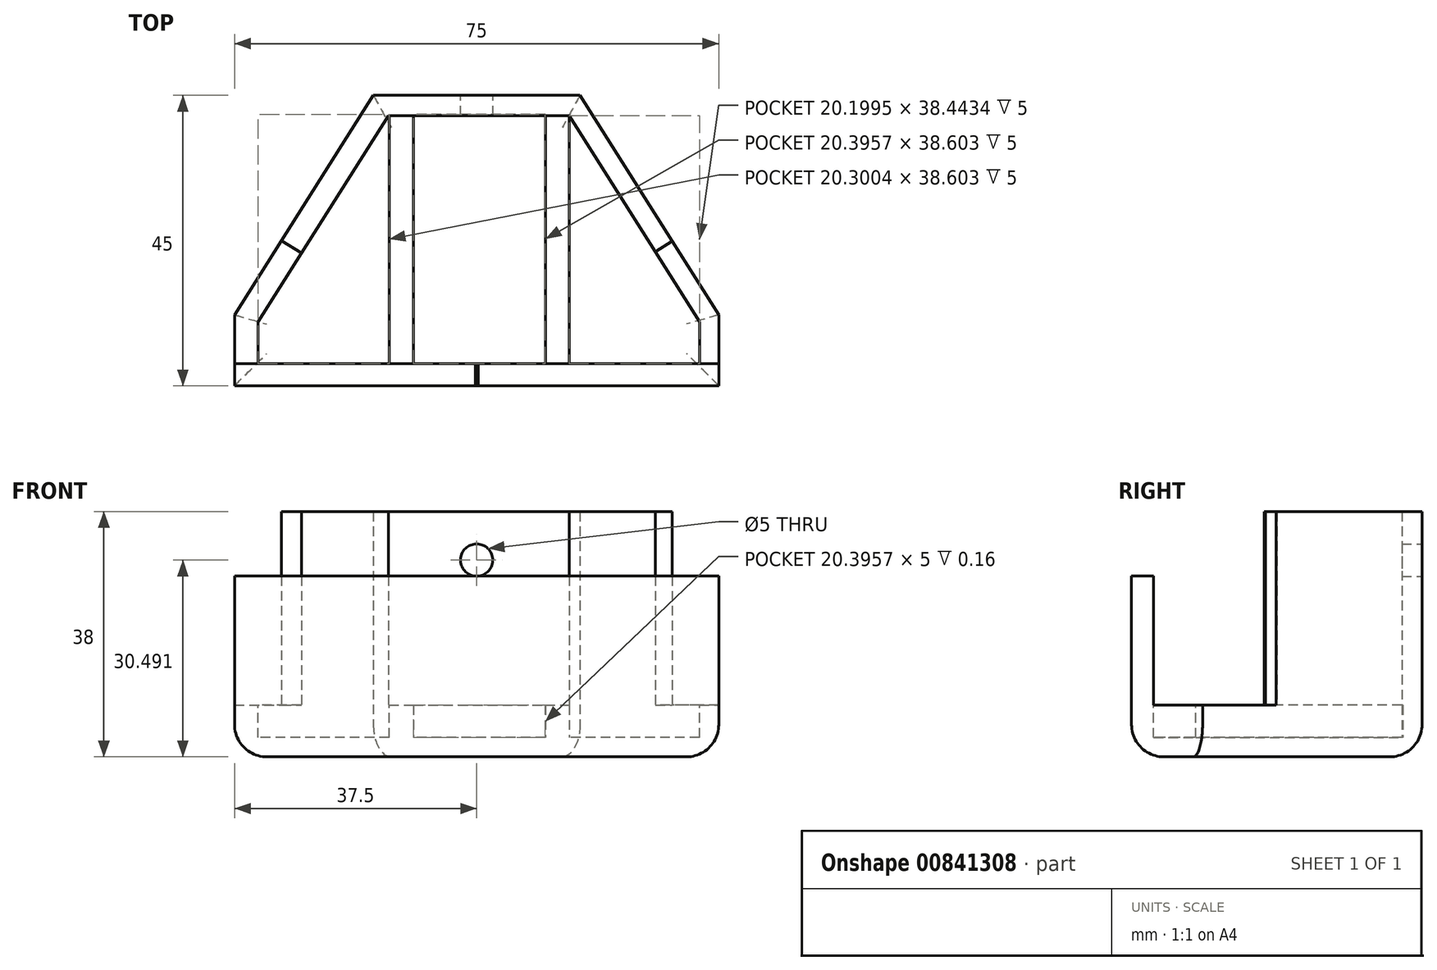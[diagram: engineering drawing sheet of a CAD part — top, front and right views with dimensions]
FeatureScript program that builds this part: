
annotation { "Feature Type Name" : "Feature", "Feature Type Description" : "" }
export const myFeature = defineFeature(function(context is Context, id is Id, definition is map)
    precondition{}
    {
        {
            var Q0;
            Q0=qCreatedBy(makeId("Top.planeOp"),FACE);
            var sketch = newSketch(context, id + "F0", { "sketchPlane" : qUnion([Q0])});
            skLineSegment(sketch, "E0.bottom", {"start": v(37.5, -22.5) * mm, "end": v(-37.5, -22.5) * mm});
            skLineSegment(sketch, "E0.top", {"start": v(16, 22.5) * mm, "end": v(-16, 22.5) * mm});
            skLineSegment(sketch, "E0.left", {"start": v(37.5, -22.5) * mm, "end": v(37.5, -11.5) * mm});
            skLineSegment(sketch, "E0.right", {"start": v(-37.5, -22.5) * mm, "end": v(-37.5, -11.5) * mm});
            skPoint(sketch, "E0.middle", {"position": v(0, 0) * mm});
            skLineSegment(sketch, "E1", {"start": v(-37.5, -11.5) * mm, "end": v(-16, 22.5) * mm});
            skLineSegment(sketch, "E2", {"start": v(37.5, -11.5) * mm, "end": v(16, 22.5) * mm});
            skPoint(sketch, "E3.orphan", {"position": v(-37.5, 22.5) * mm});
            skPoint(sketch, "E4.orphan", {"position": v(37.5, 22.5) * mm});
            skSolve(sketch);
        }
        {
            var Q0;
            Q0=makeQuery(id+"F0.imprint","IMPRINT",FACE,{"disambiguationData":[TD([[makeQuery(id+"F0.imprint","IMPRINT",EDGE,{"derivedFrom":sQuery(id+"F0.wireOp",EDGE,"E0.bottom")}),-1.0]])]});
            extrude(context, id + "F1", {"entities" : qUnion([Q0]), "depth" : 8 * mm, "offsetDistance" : 25 * mm});
        }
        {
            var Q0;
            Q0=makeQuery(id+"F1.opExtrude","CAP_FACE",FACE,{"disambiguationData":[OSD([sQuery(id+"F0.wireOp",EDGE,"E0.bottom"),sQuery(id+"F0.wireOp",EDGE,"E0.top"),sQuery(id+"F0.wireOp",EDGE,"E0.left"),sQuery(id+"F0.wireOp",EDGE,"E0.right"),sQuery(id+"F0.wireOp",EDGE,"E1"),sQuery(id+"F0.wireOp",EDGE,"E2")])],"isStart":false});
            var sketch = newSketch(context, id + "F2", { "sketchPlane" : qUnion([Q0])});
            skLineSegment(sketch, "E5", {"start": v(-33.85, -12.58) * mm, "end": v(-33.85, -19.08) * mm});
            skLineSegment(sketch, "E6", {"start": v(-33.85, -19.08) * mm, "end": v(34.5, -19.08) * mm});
            skLineSegment(sketch, "E7", {"start": v(34.5, -19.08) * mm, "end": v(34.5, -12.58) * mm});
            skLineSegment(sketch, "E8", {"start": v(34.5, -12.58) * mm, "end": v(14.2, 19.53) * mm});
            skLineSegment(sketch, "E9", {"start": v(14.2, 19.53) * mm, "end": v(-13.55, 19.53) * mm});
            skLineSegment(sketch, "E10", {"start": v(-13.55, 19.53) * mm, "end": v(-33.85, -12.58) * mm});
            skSolve(sketch);
        }
        {
            var Q0;
            Q0 = qSketchRegion(id + "F2", true);
            extrude(context, id + "F3", {"entities" : qUnion([Q0]), "operationType" : NewBodyOperationType.REMOVE, "oppositeDirection" : true, "depth" : 5 * mm, "offsetDistance" : 25 * mm});
        }
        {
            var Q0;
            Q0=makeQuery(id+"F3.boolean.opBoolean","COPY",FACE,{"derivedFrom":makeQuery(id+"F3.opExtrude","CAP_FACE",FACE,{"disambiguationData":[OSD([sQuery(id+"F2.wireOp",EDGE,"E5"),sQuery(id+"F2.wireOp",EDGE,"E6"),sQuery(id+"F2.wireOp",EDGE,"E7"),sQuery(id+"F2.wireOp",EDGE,"E8"),sQuery(id+"F2.wireOp",EDGE,"E9"),sQuery(id+"F2.wireOp",EDGE,"E10")])],"isStart":false})});
            var sketch = newSketch(context, id + "F4", { "sketchPlane" : qUnion([Q0])});
            skLineSegment(sketch, "E11.bottom", {"start": v(-9.77, 19.53) * mm, "end": v(-13.55, 19.53) * mm});
            skLineSegment(sketch, "E11.top", {"start": v(-9.77, -19.08) * mm, "end": v(-13.55, -19.08) * mm});
            skLineSegment(sketch, "E11.left", {"start": v(-9.77, 19.53) * mm, "end": v(-9.77, -19.08) * mm});
            skLineSegment(sketch, "E11.right", {"start": v(-13.55, 19.53) * mm, "end": v(-13.55, -19.08) * mm});
            skLineSegment(sketch, "E12.bottom", {"start": v(10.62, 19.53) * mm, "end": v(14.3, 19.53) * mm});
            skLineSegment(sketch, "E12.top", {"start": v(10.62, -19.08) * mm, "end": v(14.3, -19.08) * mm});
            skLineSegment(sketch, "E12.left", {"start": v(10.62, 19.53) * mm, "end": v(10.62, -19.08) * mm});
            skLineSegment(sketch, "E12.right", {"start": v(14.3, 19.53) * mm, "end": v(14.3, -19.08) * mm});
            skSolve(sketch);
        }
        {
            var Q0;
            Q0 = qSketchRegion(id + "F4", true);
            extrude(context, id + "F5", {"entities" : qUnion([Q0]), "operationType" : NewBodyOperationType.ADD, "depth" : 5 * mm, "offsetDistance" : 25 * mm});
        }
        {
            var Q0;
            Q0=makeQuery(id+"F5.boolean.opBoolean","MERGE",FACE,{"derivedFrom":[makeQuery(id+"F1.opExtrude","CAP_FACE",FACE,{"disambiguationData":[OSD([sQuery(id+"F0.wireOp",EDGE,"E0.bottom"),sQuery(id+"F0.wireOp",EDGE,"E0.top"),sQuery(id+"F0.wireOp",EDGE,"E0.left"),sQuery(id+"F0.wireOp",EDGE,"E0.right"),sQuery(id+"F0.wireOp",EDGE,"E1"),sQuery(id+"F0.wireOp",EDGE,"E2")])],"isStart":false}),makeQuery(id+"F5.opExtrude","CAP_FACE",FACE,{"disambiguationData":[OSD([sQuery(id+"F4.wireOp",EDGE,"E11.bottom"),sQuery(id+"F4.wireOp",EDGE,"E11.top"),sQuery(id+"F4.wireOp",EDGE,"E11.left"),sQuery(id+"F4.wireOp",EDGE,"E11.right")])],"isStart":false}),makeQuery(id+"F5.opExtrude","CAP_FACE",FACE,{"disambiguationData":[OSD([sQuery(id+"F4.wireOp",EDGE,"E12.bottom"),sQuery(id+"F4.wireOp",EDGE,"E12.top"),sQuery(id+"F4.wireOp",EDGE,"E12.left"),sQuery(id+"F4.wireOp",EDGE,"E12.right")])],"isStart":false})]});
            var sketch = newSketch(context, id + "F6", { "sketchPlane" : qUnion([Q0])});
            skLineSegment(sketch, "E13.bottom", {"start": v(-37.5, -22.5) * mm, "end": v(37.5, -22.5) * mm});
            skLineSegment(sketch, "E13.top", {"start": v(-37.5, -19.08) * mm, "end": v(37.5, -19.08) * mm});
            skLineSegment(sketch, "E13.left", {"start": v(-37.5, -22.5) * mm, "end": v(-37.5, -19.08) * mm});
            skLineSegment(sketch, "E13.right", {"start": v(37.5, -22.5) * mm, "end": v(37.5, -19.08) * mm});
            skSolve(sketch);
        }
        {
            var Q0;
            Q0 = qSketchRegion(id + "F6", true);
            extrude(context, id + "F7", {"entities" : qUnion([Q0]), "operationType" : NewBodyOperationType.ADD, "depth" : 20 * mm, "offsetDistance" : 25 * mm});
        }
        {
            var Q0;
            Q0=makeQuery(id+"F5.boolean.opBoolean","MERGE",FACE,{"derivedFrom":[makeQuery(id+"F1.opExtrude","CAP_FACE",FACE,{"disambiguationData":[OSD([sQuery(id+"F0.wireOp",EDGE,"E0.bottom"),sQuery(id+"F0.wireOp",EDGE,"E0.top"),sQuery(id+"F0.wireOp",EDGE,"E0.left"),sQuery(id+"F0.wireOp",EDGE,"E0.right"),sQuery(id+"F0.wireOp",EDGE,"E1"),sQuery(id+"F0.wireOp",EDGE,"E2")])],"isStart":false}),makeQuery(id+"F5.opExtrude","CAP_FACE",FACE,{"disambiguationData":[OSD([sQuery(id+"F4.wireOp",EDGE,"E11.bottom"),sQuery(id+"F4.wireOp",EDGE,"E11.top"),sQuery(id+"F4.wireOp",EDGE,"E11.left"),sQuery(id+"F4.wireOp",EDGE,"E11.right")])],"isStart":false}),makeQuery(id+"F5.opExtrude","CAP_FACE",FACE,{"disambiguationData":[OSD([sQuery(id+"F4.wireOp",EDGE,"E12.bottom"),sQuery(id+"F4.wireOp",EDGE,"E12.top"),sQuery(id+"F4.wireOp",EDGE,"E12.left"),sQuery(id+"F4.wireOp",EDGE,"E12.right")])],"isStart":false})]});
            var sketch = newSketch(context, id + "F8", { "sketchPlane" : qUnion([Q0])});
            skLineSegment(sketch, "E14.bottom", {"start": v(-16, 22.5) * mm, "end": v(16, 22.5) * mm});
            skLineSegment(sketch, "E14.top", {"start": v(-16, 19.37) * mm, "end": v(16, 19.37) * mm});
            skLineSegment(sketch, "E14.left", {"start": v(-16, 22.5) * mm, "end": v(-16, 19.37) * mm});
            skLineSegment(sketch, "E14.right", {"start": v(16, 22.5) * mm, "end": v(16, 19.37) * mm});
            skSolve(sketch);
        }
        {
            var Q0;
            Q0 = qSketchRegion(id + "F8", true);
            extrude(context, id + "F9", {"entities" : qUnion([Q0]), "operationType" : NewBodyOperationType.ADD, "depth" : 30 * mm, "offsetDistance" : 25 * mm});
        }
        {
            var Q0;
            {var subQ0=sQuery(id+"F0.wireOp",EDGE,"E0.top");var subQ4=sQuery(id+"F0.wireOp",EDGE,"E1");var subQ5=sQuery(id+"F0.wireOp",EDGE,"E0.right");Q0=makeQuery(id+"F9.boolean.opBoolean","SPLIT",FACE,{"disambiguationData":[TD([makeQuery(id+"F1.opExtrude","SWEPT_FACE",FACE,{"disambiguationData":[OSD([subQ5])]})])],"derivedFrom":makeQuery(id+"F5.boolean.opBoolean","MERGE",FACE,{"derivedFrom":[makeQuery(id+"F1.opExtrude","CAP_FACE",FACE,{"disambiguationData":[OSD([sQuery(id+"F0.wireOp",EDGE,"E0.bottom"),subQ0,sQuery(id+"F0.wireOp",EDGE,"E0.left"),subQ5,subQ4,sQuery(id+"F0.wireOp",EDGE,"E2")])],"isStart":false}),makeQuery(id+"F5.opExtrude","CAP_FACE",FACE,{"disambiguationData":[OSD([sQuery(id+"F4.wireOp",EDGE,"E11.bottom"),sQuery(id+"F4.wireOp",EDGE,"E11.top"),sQuery(id+"F4.wireOp",EDGE,"E11.left"),sQuery(id+"F4.wireOp",EDGE,"E11.right")])],"isStart":false}),makeQuery(id+"F5.opExtrude","CAP_FACE",FACE,{"disambiguationData":[OSD([sQuery(id+"F4.wireOp",EDGE,"E12.bottom"),sQuery(id+"F4.wireOp",EDGE,"E12.top"),sQuery(id+"F4.wireOp",EDGE,"E12.left"),sQuery(id+"F4.wireOp",EDGE,"E12.right")])],"isStart":false})]})});}
            var sketch = newSketch(context, id + "F10", { "sketchPlane" : qUnion([Q0])});
            skLineSegment(sketch, "E15", {"start": v(-16, 22.5) * mm, "end": v(-30.23, 0) * mm});
            skLineSegment(sketch, "E16", {"start": v(-30.23, 0) * mm, "end": v(-27.13, -1.96) * mm});
            skLineSegment(sketch, "E17", {"start": v(-27.13, -1.96) * mm, "end": v(-13.65, 19.37) * mm});
            skLineSegment(sketch, "E18", {"start": v(-13.65, 19.37) * mm, "end": v(-16, 22.5) * mm});
            skSolve(sketch);
        }
        {
            var Q0;
            Q0 = qSketchRegion(id + "F10", true);
            extrude(context, id + "F11", {"entities" : qUnion([Q0]), "operationType" : NewBodyOperationType.ADD, "depth" : 30 * mm, "offsetDistance" : 25 * mm});
        }
        {
            var Q0;
            {var subQ0=sQuery(id+"F4.wireOp",EDGE,"E12.right");var subQ1=makeQuery(id+"F5.opExtrude","CAP_FACE",FACE,{"disambiguationData":[OSD([sQuery(id+"F4.wireOp",EDGE,"E11.bottom"),sQuery(id+"F4.wireOp",EDGE,"E11.top"),sQuery(id+"F4.wireOp",EDGE,"E11.left"),sQuery(id+"F4.wireOp",EDGE,"E11.right")])],"isStart":false});var subQ2=sQuery(id+"F0.wireOp",EDGE,"E2");var subQ3=sQuery(id+"F0.wireOp",EDGE,"E0.left");var subQ4=sQuery(id+"F0.wireOp",EDGE,"E0.top");var subQ5=makeQuery(id+"F1.opExtrude","CAP_FACE",FACE,{"disambiguationData":[OSD([sQuery(id+"F0.wireOp",EDGE,"E0.bottom"),subQ4,subQ3,sQuery(id+"F0.wireOp",EDGE,"E0.right"),sQuery(id+"F0.wireOp",EDGE,"E1"),subQ2])],"isStart":false});var subQ6=makeQuery(id+"F5.opExtrude","CAP_FACE",FACE,{"disambiguationData":[OSD([sQuery(id+"F4.wireOp",EDGE,"E12.bottom"),sQuery(id+"F4.wireOp",EDGE,"E12.top"),sQuery(id+"F4.wireOp",EDGE,"E12.left"),subQ0])],"isStart":false});Q0=makeQuery(id+"F9.boolean.opBoolean","SPLIT",FACE,{"disambiguationData":[TD([makeQuery(id+"F1.opExtrude","SWEPT_FACE",FACE,{"disambiguationData":[OSD([subQ3])]})])],"derivedFrom":makeQuery(id+"F5.boolean.opBoolean","MERGE",FACE,{"derivedFrom":[subQ5,subQ1,subQ6]})});}
            var sketch = newSketch(context, id + "F12", { "sketchPlane" : qUnion([Q0])});
            skLineSegment(sketch, "E19", {"start": v(14.3, 19.37) * mm, "end": v(27.67, -1.76) * mm});
            skLineSegment(sketch, "E20", {"start": v(27.67, -1.76) * mm, "end": v(30.3, -0.1) * mm});
            skLineSegment(sketch, "E21", {"start": v(30.3, -0.1) * mm, "end": v(16, 22.5) * mm});
            skLineSegment(sketch, "E22", {"start": v(16, 22.5) * mm, "end": v(14.3, 19.37) * mm});
            skSolve(sketch);
        }
        {
            var Q0;
            Q0 = qSketchRegion(id + "F12", true);
            extrude(context, id + "F13", {"entities" : qUnion([Q0]), "operationType" : NewBodyOperationType.ADD, "depth" : 30 * mm, "offsetDistance" : 25 * mm});
        }
        {
            var Q0;
            Q0=makeQuery(id+"F1.opExtrude","CAP_EDGE",EDGE,{"disambiguationData":[OSD([sQuery(id+"F0.wireOp",EDGE,"E0.bottom")])],"isStart":true});
            var Q1;
            Q1=makeQuery(id+"F1.opExtrude","CAP_EDGE",EDGE,{"disambiguationData":[OSD([sQuery(id+"F0.wireOp",EDGE,"E0.right")])],"isStart":true});
            var Q2;
            Q2=makeQuery(id+"F1.opExtrude","CAP_EDGE",EDGE,{"disambiguationData":[OSD([sQuery(id+"F0.wireOp",EDGE,"E0.left")])],"isStart":true});
            var Q3;
            Q3=makeQuery(id+"F1.opExtrude","CAP_EDGE",EDGE,{"disambiguationData":[OSD([sQuery(id+"F0.wireOp",EDGE,"E2")])],"isStart":true});
            var Q4;
            Q4=makeQuery(id+"F1.opExtrude","CAP_EDGE",EDGE,{"disambiguationData":[OSD([sQuery(id+"F0.wireOp",EDGE,"E0.top")])],"isStart":true});
            var Q5;
            Q5=makeQuery(id+"F1.opExtrude","CAP_EDGE",EDGE,{"disambiguationData":[OSD([sQuery(id+"F0.wireOp",EDGE,"E1")])],"isStart":true});
            fillet(context, id + "F14", {"entities" : qUnion([Q0, Q1, Q2, Q3, Q4, Q5]), "radius" : 5 * mm, "tangentPropagation" : true, "allowEdgeOverflow" : false});
        }
        {
            var Q0;
            Q0=makeQuery(id+"F9.boolean.opBoolean","MERGE",FACE,{"derivedFrom":[makeQuery(id+"F1.opExtrude","SWEPT_FACE",FACE,{"disambiguationData":[OSD([sQuery(id+"F0.wireOp",EDGE,"E0.top")])]}),makeQuery(id+"F9.opExtrude","SWEPT_FACE",FACE,{"disambiguationData":[OSD([sQuery(id+"F8.wireOp",EDGE,"E14.bottom")])]})]});
            var sketch = newSketch(context, id + "F15", { "sketchPlane" : qUnion([Q0])});
            skCircle(sketch, "E23", {"center": v(0, 30.5) * mm, "radius": 2.5 * mm});
            skSolve(sketch);
        }
        {
            var Q0;
            Q0=sQuery(id+"F15.wireOp",VERTEX,"E23.center");
            var Q1;
            Q1=makeQuery(id+"F1.opExtrude","SWEPT_BODY",BODY,{"disambiguationData":[OSD([sQuery(id+"F0.wireOp",EDGE,"E0.bottom"),sQuery(id+"F0.wireOp",EDGE,"E0.top"),sQuery(id+"F0.wireOp",EDGE,"E0.left"),sQuery(id+"F0.wireOp",EDGE,"E0.right"),sQuery(id+"F0.wireOp",EDGE,"E1"),sQuery(id+"F0.wireOp",EDGE,"E2")])]});
            hole(context, id + "F16", {"style" : HoleStyle.SIMPLE, "endStyle" : HoleEndStyle.THROUGH, "holeDiameter" : 5 * mm, "majorDiameter" : 5 * mm, "isTappedThrough" : true, "tappedDepth" : 12 * mm, "tapClearance" : 3, "locations" : qUnion([Q0]), "scope" : qUnion([Q1])});
        }
    });
